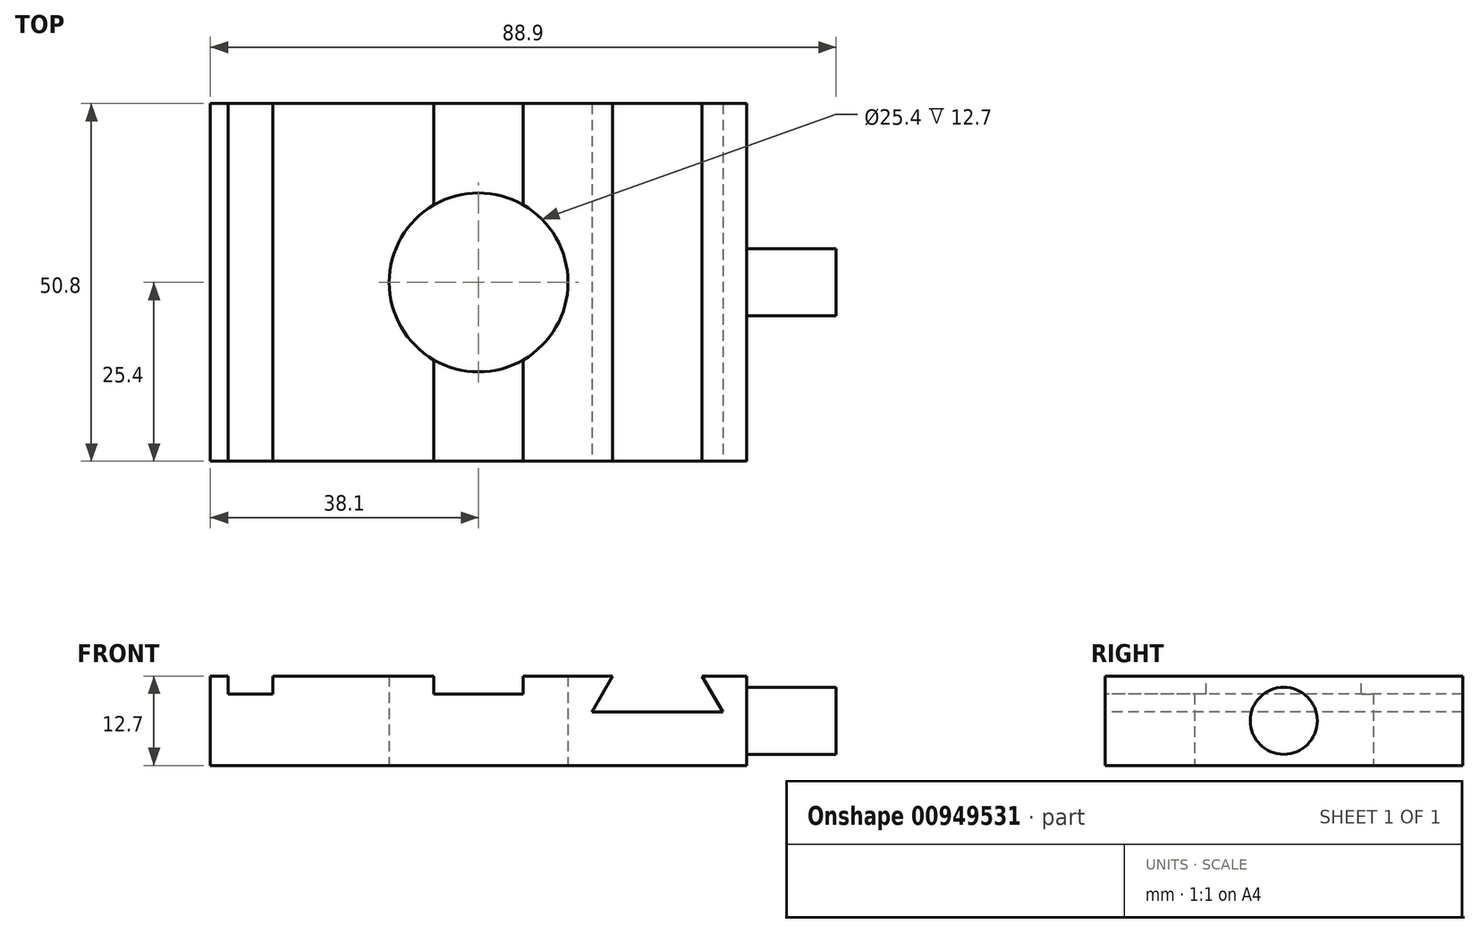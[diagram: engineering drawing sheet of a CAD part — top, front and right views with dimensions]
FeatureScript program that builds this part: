
annotation { "Feature Type Name" : "Feature", "Feature Type Description" : "" }
export const myFeature = defineFeature(function(context is Context, id is Id, definition is map)
    precondition{}
    {
        {
            var Q0;
            Q0=qCreatedBy(makeId("Top.planeOp"),FACE);
            var sketch = newSketch(context, id + "F0", { "sketchPlane" : qUnion([Q0])});
            skLineSegment(sketch, "E0.bottom", {"start": v(38.1, -25.4) * mm, "end": v(-38.1, -25.4) * mm});
            skLineSegment(sketch, "E0.top", {"start": v(38.1, 25.4) * mm, "end": v(-38.1, 25.4) * mm});
            skLineSegment(sketch, "E0.left", {"start": v(38.1, -25.4) * mm, "end": v(38.1, 25.4) * mm});
            skLineSegment(sketch, "E0.right", {"start": v(-38.1, -25.4) * mm, "end": v(-38.1, 25.4) * mm});
            skPoint(sketch, "E0.middle", {"position": v(0, 0) * mm});
            skCircle(sketch, "E1", {"center": v(0, 0) * mm, "radius": 12.7 * mm});
            skSolve(sketch);
        }
        {
            var Q0;
            Q0=makeQuery(id+"F0.imprint","IMPRINT",FACE,{"disambiguationData":[TD([[makeQuery(id+"F0.imprint","IMPRINT",EDGE,{"derivedFrom":sQuery(id+"F0.wireOp",EDGE,"E0.bottom")}),-1.0]])]});
            extrude(context, id + "F1", {"entities" : qUnion([Q0]), "depth" : 12.7 * mm, "offsetDistance" : 25.4 * mm});
        }
        {
            var Q0;
            Q0=makeQuery(id+"F1.opExtrude","CAP_FACE",FACE,{"disambiguationData":[OSD([sQuery(id+"F0.wireOp",EDGE,"E0.bottom"),sQuery(id+"F0.wireOp",EDGE,"E0.top"),sQuery(id+"F0.wireOp",EDGE,"E0.left"),sQuery(id+"F0.wireOp",EDGE,"E0.right"),sQuery(id+"F0.wireOp",EDGE,"E1")])],"isStart":false});
            var sketch = newSketch(context, id + "F2", { "sketchPlane" : qUnion([Q0])});
            skLineSegment(sketch, "E2.bottom", {"start": v(-35.56, 25.4) * mm, "end": v(-29.2, 25.4) * mm});
            skLineSegment(sketch, "E2.top", {"start": v(-35.56, -25.4) * mm, "end": v(-29.2, -25.4) * mm});
            skLineSegment(sketch, "E2.left", {"start": v(-35.56, 25.4) * mm, "end": v(-35.56, -25.4) * mm});
            skLineSegment(sketch, "E2.right", {"start": v(-29.2, 25.4) * mm, "end": v(-29.2, -25.4) * mm});
            skLineSegment(sketch, "E3", {"start": v(-6.35, 25.4) * mm, "end": v(-6.35, -25.4) * mm});
            skPoint(sketch, "E3.endSnap0", {"position": v(0, -25.4) * mm});
            skLineSegment(sketch, "E4", {"start": v(6.35, -25.4) * mm, "end": v(6.35, 25.4) * mm});
            skLineSegment(sketch, "E5", {"start": v(6.35, 25.4) * mm, "end": v(-6.35, 25.4) * mm});
            skPoint(sketch, "E6", {"position": v(0, 0) * mm});
            skLineSegment(sketch, "E7", {"start": v(0, 25.4) * mm, "end": v(0, -25.4) * mm, "construction": true});
            skSolve(sketch);
        }
        {
            var Q0;
            Q0=makeQuery(id+"F2.imprint","IMPRINT",FACE,{"disambiguationData":[TD([[makeQuery(id+"F2.imprint","IMPRINT",EDGE,{"derivedFrom":sQuery(id+"F2.wireOp",EDGE,"E2.bottom")}),1.0]])]});
            var Q1;
            {var subQ0=sQuery(id+"F2.wireOp",EDGE,"E3");var subQ1=makeQuery(id+"F1.opExtrude","CAP_EDGE",EDGE,{"disambiguationData":[OSD([sQuery(id+"F0.wireOp",EDGE,"E0.bottom")])],"isStart":false});var subQ2=makeQuery(id+"F2.imprint","INTERSECT",VERTEX,{"derivedFrom":[subQ1,subQ0]});Q1=makeQuery(id+"F2.imprint","IMPRINT",FACE,{"disambiguationData":[TD([[makeQuery(id+"F2.imprint","IMPRINT",EDGE,{"disambiguationData":[TD([[subQ2,1.0]])],"derivedFrom":subQ0}),1.0]])]});}
            var Q2;
            {var subQ0=sQuery(id+"F2.wireOp",EDGE,"E5");Q2=makeQuery(id+"F2.imprint","IMPRINT",FACE,{"disambiguationData":[TD([[makeQuery(id+"F2.imprint","IMPRINT",EDGE,{"derivedFrom":subQ0}),1.0]])]});}
            extrude(context, id + "F3", {"entities" : qUnion([Q0, Q1, Q2]), "operationType" : NewBodyOperationType.REMOVE, "oppositeDirection" : true, "depth" : 2.54 * mm, "offsetDistance" : 25.4 * mm});
        }
        {
            var Q0;
            Q0=makeQuery(id+"F1.opExtrude","SWEPT_FACE",FACE,{"disambiguationData":[OSD([sQuery(id+"F0.wireOp",EDGE,"E0.bottom")])]});
            var sketch = newSketch(context, id + "F4", { "sketchPlane" : qUnion([Q0])});
            skLineSegment(sketch, "E8", {"start": v(19.05, 12.7) * mm, "end": v(16.12, 7.62) * mm});
            skLineSegment(sketch, "E9", {"start": v(16.12, 7.62) * mm, "end": v(34.68, 7.62) * mm});
            skLineSegment(sketch, "E10", {"start": v(34.68, 7.62) * mm, "end": v(31.75, 12.7) * mm});
            skLineSegment(sketch, "E11", {"start": v(31.75, 12.7) * mm, "end": v(19.05, 12.7) * mm});
            skLineSegment(sketch, "E12", {"start": v(25.4, 7.62) * mm, "end": v(25.4, 12.7) * mm, "construction": true});
            skSolve(sketch);
        }
        {
            var Q0;
            Q0=makeQuery(id+"F4.imprint","IMPRINT",FACE,{"disambiguationData":[TD([[makeQuery(id+"F4.imprint","IMPRINT",EDGE,{"derivedFrom":sQuery(id+"F4.wireOp",EDGE,"E8")}),1.0]])]});
            extrude(context, id + "F5", {"entities" : qUnion([Q0]), "operationType" : NewBodyOperationType.REMOVE, "endBound" : BoundingType.THROUGH_ALL, "oppositeDirection" : true, "depth" : 25.4 * mm, "offsetDistance" : 25.4 * mm});
        }
        {
            var Q0;
            Q0=makeQuery(id+"F1.opExtrude","SWEPT_FACE",FACE,{"disambiguationData":[OSD([sQuery(id+"F0.wireOp",EDGE,"E0.left")])]});
            var sketch = newSketch(context, id + "F6", { "sketchPlane" : qUnion([Q0])});
            skCircle(sketch, "E13", {"center": v(0, 6.35) * mm, "radius": 4.76 * mm});
            skPoint(sketch, "E13.centerSnap0", {"position": v(-25.4, 6.35) * mm});
            skPoint(sketch, "E13.centerSnap1", {"position": v(0, 12.7) * mm});
            skSolve(sketch);
        }
        {
            var Q0;
            Q0=makeQuery(id+"F6.imprint","IMPRINT",FACE,{"disambiguationData":[TD([[makeQuery(id+"F6.imprint","IMPRINT",EDGE,{"derivedFrom":sQuery(id+"F6.wireOp",EDGE,"E13")}),1.0]])]});
            extrude(context, id + "F7", {"entities" : qUnion([Q0]), "operationType" : NewBodyOperationType.ADD, "depth" : 12.7 * mm, "offsetDistance" : 25.4 * mm});
        }
    });
